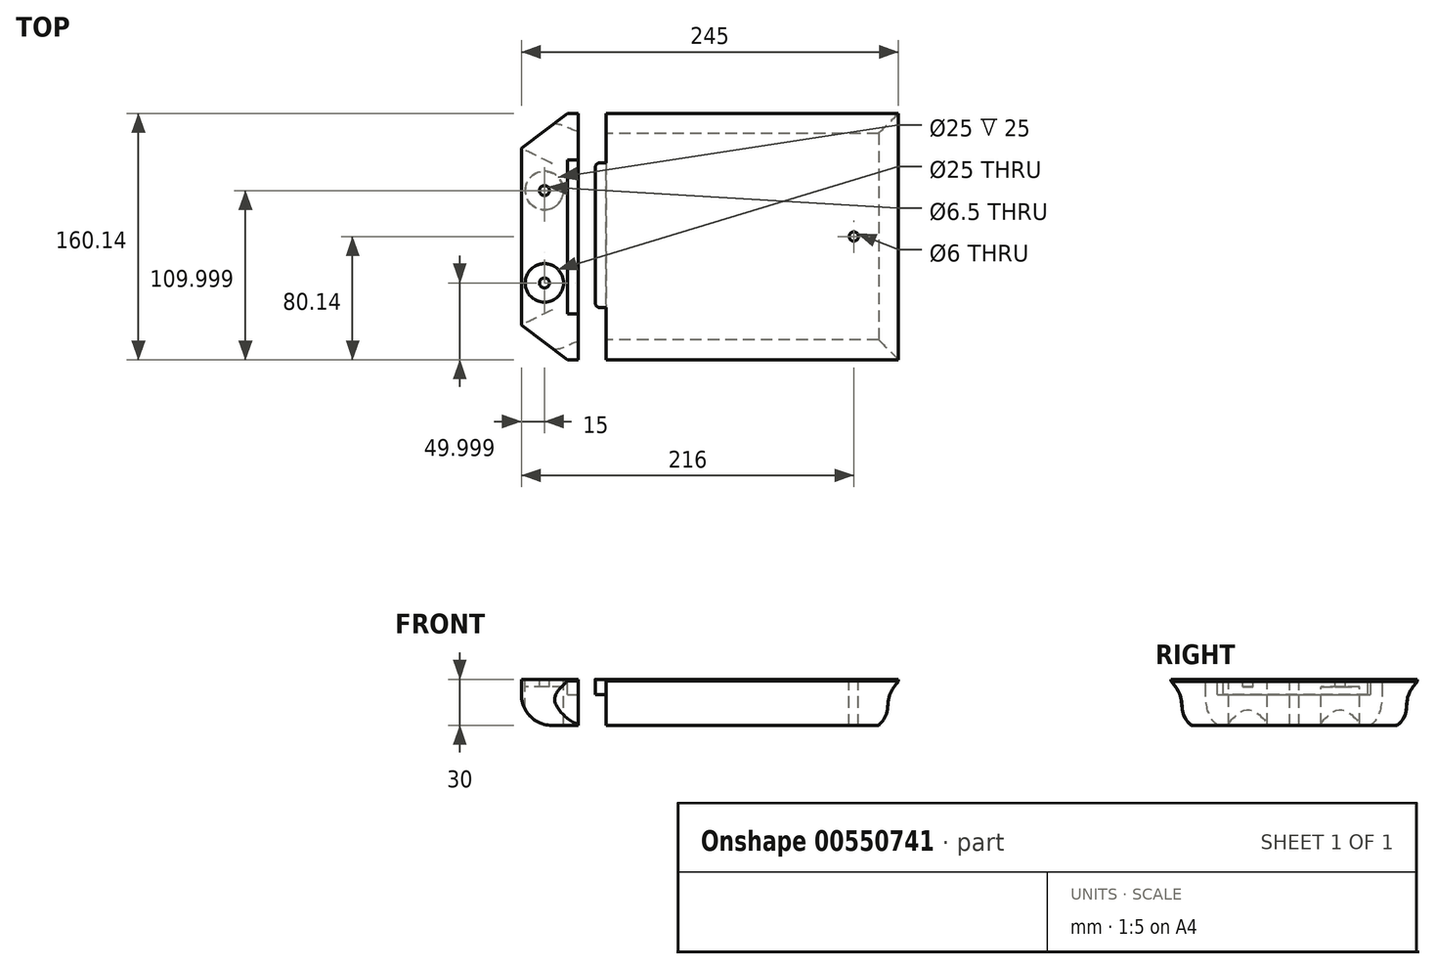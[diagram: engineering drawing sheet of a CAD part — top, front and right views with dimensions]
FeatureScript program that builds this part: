
annotation { "Feature Type Name" : "Feature", "Feature Type Description" : "" }
export const myFeature = defineFeature(function(context is Context, id is Id, definition is map)
    precondition{}
    {
        {
            var Q0;
            Q0=qCreatedBy(makeId("Top.planeOp"),FACE);
            var sketch = newSketch(context, id + "F0", { "sketchPlane" : qUnion([Q0])});
            skLineSegment(sketch, "E0.bottom", {"start": v(-97.5, 80) * mm, "end": v(92.5, 80) * mm});
            skLineSegment(sketch, "E0.top", {"start": v(-92.5, 0) * mm, "end": v(92.5, 0) * mm, "construction": true});
            skLineSegment(sketch, "E0.right", {"start": v(92.5, 80) * mm, "end": v(92.5, 0) * mm});
            skLineSegment(sketch, "E1.bottom", {"start": v(-82.5, 63.5) * mm, "end": v(77.5, 63.5) * mm});
            skLineSegment(sketch, "E1.left", {"start": v(-97.5, 63.5) * mm, "end": v(-97.5, -5) * mm});
            skLineSegment(sketch, "E1.right", {"start": v(77.5, 63.5) * mm, "end": v(77.5, 0) * mm});
            skLineSegment(sketch, "E2.right", {"start": v(49.5, 65) * mm, "end": v(49.5, 0) * mm});
            skLineSegment(sketch, "E3.MirrorCS", {"start": v(-82.5, -63.5) * mm, "end": v(77.5, -63.5) * mm});
            skLineSegment(sketch, "E4.MirrorCS", {"start": v(-97.5, -63.5) * mm, "end": v(-97.5, 5) * mm});
            skLineSegment(sketch, "E5.MirrorCS", {"start": v(-97.5, -80) * mm, "end": v(92.5, -80) * mm});
            skLineSegment(sketch, "E6.MirrorCS", {"start": v(92.5, -80) * mm, "end": v(92.5, 0) * mm});
            skLineSegment(sketch, "E7.MirrorCS", {"start": v(57.5, -4.97) * mm, "end": v(66.5, -4.97) * mm});
            skLineSegment(sketch, "E8.MirrorCS", {"start": v(54.5, -13.97) * mm, "end": v(54.5, -9.97) * mm});
            skLineSegment(sketch, "E9.MirrorCS", {"start": v(77.5, -63.5) * mm, "end": v(77.5, 0) * mm});
            skLineSegment(sketch, "E10.MirrorCS", {"start": v(69.5, -13.97) * mm, "end": v(69.5, -9.97) * mm});
            skLineSegment(sketch, "E11.MirrorCS", {"start": v(49.5, -63.5) * mm, "end": v(49.5, 0) * mm});
            skLineSegment(sketch, "E12", {"start": v(-97.5, -63.5) * mm, "end": v(-97.5, -80) * mm});
            skLineSegment(sketch, "E13", {"start": v(-97.5, 63.5) * mm, "end": v(-97.5, 80) * mm});
            skLineSegment(sketch, "E14.left", {"start": v(-152.5, 57.36) * mm, "end": v(-152.5, 9.86) * mm});
            skCircle(sketch, "E15", {"center": v(-137.5, 29.86) * mm, "radius": 3.25 * mm});
            skLineSegment(sketch, "E16.left", {"start": v(-122.5, 79.86) * mm, "end": v(-122.5, -0.14) * mm});
            skCircle(sketch, "E17.MirrorC", {"center": v(-137.5, -30.14) * mm, "radius": 3.25 * mm});
            skLineSegment(sketch, "E18.MirrorCS", {"start": v(-122.5, -80.14) * mm, "end": v(-122.5, -10.14) * mm});
            skLineSegment(sketch, "E19.MirrorCS", {"start": v(-152.5, -57.64) * mm, "end": v(-152.5, -10.14) * mm});
            skCircle(sketch, "E20", {"center": v(-137.5, 29.86) * mm, "radius": 12.5 * mm});
            skCircle(sketch, "E21.MirrorC", {"center": v(-137.5, -30.14) * mm, "radius": 12.5 * mm});
            skPoint(sketch, "E22", {"position": v(-122.5, -50.14) * mm});
            skLineSegment(sketch, "E23", {"start": v(-122.5, -50.14) * mm, "end": v(-117.5, -50.14) * mm});
            skPoint(sketch, "E24", {"position": v(-122.5, 49.86) * mm});
            skLineSegment(sketch, "E25", {"start": v(-122.5, 49.86) * mm, "end": v(-117.5, 49.86) * mm});
            skLineSegment(sketch, "E26", {"start": v(-104.5, -30.14) * mm, "end": v(-104.5, 44.86) * mm});
            skLineSegment(sketch, "E27", {"start": v(-117.5, -50.14) * mm, "end": v(-115.5, -50.14) * mm});
            skLineSegment(sketch, "E28", {"start": v(-115.5, -50.14) * mm, "end": v(-115.5, -80.14) * mm});
            skLineSegment(sketch, "E29", {"start": v(-115.5, -50.14) * mm, "end": v(-115.5, 79.86) * mm});
            skLineSegment(sketch, "E30", {"start": v(-117.5, 49.86) * mm, "end": v(-115.5, 49.86) * mm});
            skLineSegment(sketch, "E31", {"start": v(-97.5, -80) * mm, "end": v(-82.5, -80) * mm});
            skLineSegment(sketch, "E32", {"start": v(-82.5, -80) * mm, "end": v(-82.5, 63.5) * mm});
            skLineSegment(sketch, "E33", {"start": v(57.5, -16.97) * mm, "end": v(66.5, -16.97) * mm});
            skLineSegment(sketch, "E34", {"start": v(57.5, -6.97) * mm, "end": v(66.5, -6.97) * mm});
            skLineSegment(sketch, "E35", {"start": v(57.5, -18.97) * mm, "end": v(66.5, -18.97) * mm});
            skLineSegment(sketch, "E36", {"start": v(56.02, -30.47) * mm, "end": v(63.02, -30.47) * mm});
            skLineSegment(sketch, "E37", {"start": v(54.5, -63.15) * mm, "end": v(66.5, -63.15) * mm});
            skLineSegment(sketch, "E38", {"start": v(69.5, -58.47) * mm, "end": v(69.5, -51.47) * mm});
            skArc(sketch, "E39.filletArc", {"start": v(57.5, -4.97) * mm, "mid": v(55.38, -5.85) * mm, "end": v(54.5, -7.97) * mm});
            skArc(sketch, "E40.filletArc", {"start": v(69.5, -7.97) * mm, "mid": v(68.62, -5.85) * mm, "end": v(66.5, -4.97) * mm});
            skLineSegment(sketch, "E41", {"start": v(54.5, -45) * mm, "end": v(54.5, -27.47) * mm});
            skLineSegment(sketch, "E42", {"start": v(69.5, -27.47) * mm, "end": v(69.5, -45) * mm});
            skCircle(sketch, "E43", {"center": v(62, -55.5) * mm, "radius": 2.55 * mm});
            skCircle(sketch, "E44.MirrorC", {"center": v(62, 25.97) * mm, "radius": 2.55 * mm});
            skLineSegment(sketch, "E45.MirrorCS", {"start": v(57.5, 6.97) * mm, "end": v(66.5, 6.97) * mm});
            skLineSegment(sketch, "E46.MirrorCS", {"start": v(69.5, 13.97) * mm, "end": v(69.5, 9.97) * mm});
            skLineSegment(sketch, "E47.MirrorCS", {"start": v(57.5, 16.97) * mm, "end": v(66.5, 16.97) * mm});
            skLineSegment(sketch, "E48.MirrorCS", {"start": v(57.5, 4.97) * mm, "end": v(66.5, 4.97) * mm});
            skLineSegment(sketch, "E49.MirrorCS", {"start": v(57.5, 18.97) * mm, "end": v(66.5, 18.97) * mm});
            skLineSegment(sketch, "E50.MirrorCS", {"start": v(54.5, 44.51) * mm, "end": v(54.5, 27.47) * mm});
            skLineSegment(sketch, "E51.MirrorCS", {"start": v(69.5, 27.47) * mm, "end": v(69.5, 44.51) * mm});
            skLineSegment(sketch, "E52.MirrorCS", {"start": v(54.5, 15.97) * mm, "end": v(54.5, 9.97) * mm});
            skLineSegment(sketch, "E53.MirrorCS", {"start": v(69.5, 15.97) * mm, "end": v(69.5, 7.97) * mm});
            skLineSegment(sketch, "E54.MirrorCS", {"start": v(57.5, 6.97) * mm, "end": v(65.5, 6.97) * mm});
            skLineSegment(sketch, "E55.MirrorCS", {"start": v(54.5, 16.97) * mm, "end": v(54.67, 16.97) * mm});
            skLineSegment(sketch, "E56.MirrorCS", {"start": v(54.5, 13.97) * mm, "end": v(54.5, 7.97) * mm});
            skLineSegment(sketch, "E57.MirrorCS", {"start": v(57.5, 18.97) * mm, "end": v(65.5, 18.97) * mm});
            skLineSegment(sketch, "E58", {"start": v(57.5, 47.51) * mm, "end": v(66.5, 47.51) * mm});
            skLineSegment(sketch, "E59", {"start": v(54.5, -49.9) * mm, "end": v(67.5, -49.9) * mm});
            skLineSegment(sketch, "E60", {"start": v(-122.5, 79.86) * mm, "end": v(-115.5, 79.86) * mm});
            skLineSegment(sketch, "E61", {"start": v(-122.5, -80.14) * mm, "end": v(-115.5, -80.14) * mm});
            skLineSegment(sketch, "E62", {"start": v(-122.5, 79.86) * mm, "end": v(-152.5, 57.36) * mm});
            skLineSegment(sketch, "E63", {"start": v(-122.5, -80.14) * mm, "end": v(-152.5, -57.64) * mm});
            skLineSegment(sketch, "E64", {"start": v(49.5, 41) * mm, "end": v(54.5, 41) * mm});
            skLineSegment(sketch, "E65", {"start": v(49.5, 29) * mm, "end": v(54.5, 29) * mm});
            skLineSegment(sketch, "E66", {"start": v(77.5, 0) * mm, "end": v(49.5, 0) * mm});
            skCircle(sketch, "E67", {"center": v(63.5, 0) * mm, "radius": 3 * mm});
            skLineSegment(sketch, "E68", {"start": v(57.9, 23.83) * mm, "end": v(57.9, 28.1) * mm});
            skLineSegment(sketch, "E69", {"start": v(66.1, 23.83) * mm, "end": v(66.1, 28.1) * mm});
            skLineSegment(sketch, "E70", {"start": v(60.28, 21.42) * mm, "end": v(57.9, 23.08) * mm});
            skLineSegment(sketch, "E71", {"start": v(63.72, 21.42) * mm, "end": v(66.1, 23.08) * mm});
            skLineSegment(sketch, "E72", {"start": v(63.72, 30.52) * mm, "end": v(66.1, 28.86) * mm});
            skLineSegment(sketch, "E73", {"start": v(60.28, 30.52) * mm, "end": v(57.9, 28.86) * mm});
            skLineSegment(sketch, "E74", {"start": v(57.9, -57.64) * mm, "end": v(57.9, -53.37) * mm});
            skLineSegment(sketch, "E75", {"start": v(66.1, -57.64) * mm, "end": v(66.1, -53.37) * mm});
            skLineSegment(sketch, "E76", {"start": v(60.28, -60.05) * mm, "end": v(57.9, -58.4) * mm});
            skLineSegment(sketch, "E77", {"start": v(63.72, -60.05) * mm, "end": v(66.1, -58.4) * mm});
            skLineSegment(sketch, "E78", {"start": v(63.72, -50.94) * mm, "end": v(66.1, -52.6) * mm});
            skLineSegment(sketch, "E79", {"start": v(60.28, -50.94) * mm, "end": v(57.9, -52.6) * mm});
            skCircle(sketch, "E80.MirrorC", {"center": v(62, -24.47) * mm, "radius": 2.55 * mm});
            skLineSegment(sketch, "E81", {"start": v(57.9, -26.61) * mm, "end": v(57.9, -22.33) * mm});
            skLineSegment(sketch, "E82", {"start": v(66.1, -26.61) * mm, "end": v(66.1, -22.33) * mm});
            skLineSegment(sketch, "E83", {"start": v(60.28, -29.02) * mm, "end": v(57.9, -27.36) * mm});
            skLineSegment(sketch, "E84", {"start": v(63.72, -29.02) * mm, "end": v(66.1, -27.36) * mm});
            skLineSegment(sketch, "E85", {"start": v(63.72, -19.92) * mm, "end": v(66.1, -21.58) * mm});
            skLineSegment(sketch, "E86", {"start": v(60.28, -19.92) * mm, "end": v(57.9, -21.58) * mm});
            skArc(sketch, "E87.filletArc", {"start": v(69.5, 44.51) * mm, "mid": v(68.62, 46.63) * mm, "end": v(66.5, 47.51) * mm});
            skArc(sketch, "E88.filletArc", {"start": v(57.5, 47.51) * mm, "mid": v(55.38, 46.63) * mm, "end": v(54.5, 44.51) * mm});
            skArc(sketch, "E89.filletArc", {"start": v(54.5, 9.97) * mm, "mid": v(55.38, 7.85) * mm, "end": v(57.5, 6.97) * mm});
            skArc(sketch, "E90.filletArc", {"start": v(66.5, 6.97) * mm, "mid": v(68.62, 7.85) * mm, "end": v(69.5, 9.97) * mm});
            skArc(sketch, "E91.filletArc", {"start": v(57.5, 16.97) * mm, "mid": v(55.38, 16.1) * mm, "end": v(54.5, 13.97) * mm});
            skArc(sketch, "E92.filletArc", {"start": v(69.5, 13.97) * mm, "mid": v(68.62, 16.1) * mm, "end": v(66.5, 16.97) * mm});
            skArc(sketch, "E93.filletArc", {"start": v(57.5, 18.97) * mm, "mid": v(55.38, 18.1) * mm, "end": v(54.5, 15.97) * mm});
            skArc(sketch, "E94.filletArc", {"start": v(69.5, 15.97) * mm, "mid": v(68.62, 18.1) * mm, "end": v(66.5, 18.97) * mm});
            skArc(sketch, "E95.filletArc", {"start": v(54.5, -13.97) * mm, "mid": v(55.38, -16.1) * mm, "end": v(57.5, -16.97) * mm});
            skArc(sketch, "E96.filletArc", {"start": v(66.5, -16.97) * mm, "mid": v(68.62, -16.1) * mm, "end": v(69.5, -13.97) * mm});
            skLineSegment(sketch, "E97", {"start": v(54.5, -13.97) * mm, "end": v(54.5, -15.97) * mm});
            skLineSegment(sketch, "E98", {"start": v(69.5, -13.97) * mm, "end": v(69.5, -15.97) * mm});
            skArc(sketch, "E99.filletArc", {"start": v(54.5, -15.97) * mm, "mid": v(55.38, -18.1) * mm, "end": v(57.5, -18.97) * mm});
            skArc(sketch, "E100.filletArc", {"start": v(66.5, -18.97) * mm, "mid": v(68.62, -18.1) * mm, "end": v(69.5, -15.97) * mm});
            skLineSegment(sketch, "E101", {"start": v(54.5, -15.97) * mm, "end": v(54.5, -25.97) * mm});
            skLineSegment(sketch, "E102", {"start": v(69.5, -25.97) * mm, "end": v(69.5, -15.97) * mm});
            skArc(sketch, "E103.filletArc", {"start": v(57.5, -6.97) * mm, "mid": v(55.38, -7.85) * mm, "end": v(54.5, -9.97) * mm});
            skArc(sketch, "E104.filletArc", {"start": v(69.5, -9.97) * mm, "mid": v(68.62, -7.85) * mm, "end": v(66.5, -6.97) * mm});
            skLineSegment(sketch, "E105", {"start": v(54.5, -9.97) * mm, "end": v(54.5, -7.97) * mm});
            skLineSegment(sketch, "E106", {"start": v(69.5, -9.97) * mm, "end": v(69.5, -7.97) * mm});
            skLineSegment(sketch, "E107", {"start": v(54.5, 27.47) * mm, "end": v(54.5, 13.97) * mm});
            skLineSegment(sketch, "E108", {"start": v(69.5, 27.47) * mm, "end": v(69.5, 15.97) * mm});
            skLineSegment(sketch, "E109", {"start": v(69.5, -45) * mm, "end": v(69.5, -51.47) * mm});
            skLineSegment(sketch, "E110", {"start": v(69.5, -58.47) * mm, "end": v(69.5, -60.15) * mm});
            skArc(sketch, "E111.filletArc", {"start": v(66.5, -63.15) * mm, "mid": v(68.62, -62.27) * mm, "end": v(69.5, -60.15) * mm});
            skLineSegment(sketch, "E112", {"start": v(-122.5, -10.14) * mm, "end": v(-122.5, -0.14) * mm});
            skLineSegment(sketch, "E113", {"start": v(-152.5, -10.14) * mm, "end": v(-152.5, 9.86) * mm});
            skLineSegment(sketch, "E114", {"start": v(-122.5, -50.14) * mm, "end": v(-152.5, -50.14) * mm});
            skLineSegment(sketch, "E115", {"start": v(-122.5, 49.86) * mm, "end": v(-152.5, 49.86) * mm});
            skLineSegment(sketch, "E116", {"start": v(46.5, -63.5) * mm, "end": v(46.5, 63.5) * mm});
            skLineSegment(sketch, "E117", {"start": v(56.02, -30.47) * mm, "end": v(54.5, -30.47) * mm});
            skLineSegment(sketch, "E118", {"start": v(63.02, -30.47) * mm, "end": v(69.5, -30.47) * mm});
            skLineSegment(sketch, "E119", {"start": v(49.5, 29) * mm, "end": v(46.5, 29) * mm});
            skLineSegment(sketch, "E120", {"start": v(49.5, 41) * mm, "end": v(46.5, 41) * mm});
            skLineSegment(sketch, "E121", {"start": v(50.5, -49.9) * mm, "end": v(47.5, -49.9) * mm});
            skLineSegment(sketch, "E122", {"start": v(65.5, -49.9) * mm, "end": v(55.5, -49.9) * mm});
            skLineSegment(sketch, "E123", {"start": v(54.5, -30.47) * mm, "end": v(69.5, -30.47) * mm});
            skLineSegment(sketch, "E124", {"start": v(69.5, -30.47) * mm, "end": v(69.5, -50) * mm});
            skLineSegment(sketch, "E125", {"start": v(-101.5, 47.86) * mm, "end": v(-97.5, 47.86) * mm});
            skLineSegment(sketch, "E126", {"start": v(-104.5, -30.14) * mm, "end": v(-104.5, -43.14) * mm});
            skLineSegment(sketch, "E127", {"start": v(-101.5, -46.14) * mm, "end": v(-97.5, -46.14) * mm});
            skPoint(sketch, "E128.end.orphan", {"position": v(-97.5, 59.86) * mm});
            skLineSegment(sketch, "E129", {"start": v(47.5, -49.9) * mm, "end": v(46.5, -49.9) * mm});
            skPoint(sketch, "E130", {"position": v(-90, -50) * mm});
            skLineSegment(sketch, "E131", {"start": v(-93.5, -52.14) * mm, "end": v(-93.5, -47.87) * mm});
            skLineSegment(sketch, "E132", {"start": v(-86.5, -52.14) * mm, "end": v(-86.5, -47.87) * mm});
            skLineSegment(sketch, "E133", {"start": v(-91.72, -54.89) * mm, "end": v(-93.5, -53.64) * mm});
            skLineSegment(sketch, "E134", {"start": v(-88.28, -45.12) * mm, "end": v(-86.5, -46.37) * mm});
            skLineSegment(sketch, "E135", {"start": v(-91.72, -45.12) * mm, "end": v(-93.5, -46.37) * mm});
            skLineSegment(sketch, "E136", {"start": v(-86.5, -53.64) * mm, "end": v(-88.28, -54.89) * mm});
            skPoint(sketch, "E137.newPointA", {"position": v(66.5, 4.97) * mm});
            skArc(sketch, "E137.filletArc", {"start": v(66.5, 4.97) * mm, "mid": v(68.62, 5.85) * mm, "end": v(69.5, 7.97) * mm});
            skPoint(sketch, "E138.MirrorCS.start.orphan", {"position": v(69.5, 7.97) * mm});
            skLineSegment(sketch, "E139.trimOffspring", {"start": v(57.5, 16.97) * mm, "end": v(64.5, 16.97) * mm});
            skPoint(sketch, "E140.newPointA", {"position": v(57.5, 4.97) * mm});
            skArc(sketch, "E140.filletArc", {"start": v(54.5, 7.97) * mm, "mid": v(55.38, 5.85) * mm, "end": v(57.5, 4.97) * mm});
            skPoint(sketch, "E141.MirrorCS.end.orphan", {"position": v(54.5, 7.97) * mm});
            skLineSegment(sketch, "E142", {"start": v(54.5, -45) * mm, "end": v(54.5, -63.5) * mm});
            skLineSegment(sketch, "E143", {"start": v(69.5, -25.97) * mm, "end": v(69.5, -27.47) * mm});
            skLineSegment(sketch, "E144", {"start": v(54.5, -25.97) * mm, "end": v(54.5, -27.47) * mm});
            skArc(sketch, "E145.filletArc", {"start": v(-104.5, -43.14) * mm, "mid": v(-103.62, -45.26) * mm, "end": v(-101.5, -46.14) * mm});
            skArc(sketch, "E146.filletArc", {"start": v(-101.5, 47.86) * mm, "mid": v(-103.62, 46.98) * mm, "end": v(-104.5, 44.86) * mm});
            skLineSegment(sketch, "E147", {"start": v(-93.5, -47.87) * mm, "end": v(-93.5, -46.37) * mm});
            skLineSegment(sketch, "E148", {"start": v(-86.5, -47.87) * mm, "end": v(-86.5, -46.37) * mm});
            skLineSegment(sketch, "E149", {"start": v(-93.5, -52.14) * mm, "end": v(-93.5, -53.64) * mm});
            skLineSegment(sketch, "E150", {"start": v(-86.5, -52.14) * mm, "end": v(-86.5, -53.64) * mm});
            skLineSegment(sketch, "E151.MirrorCS", {"start": v(-86.5, 52.14) * mm, "end": v(-86.5, 47.87) * mm});
            skLineSegment(sketch, "E152.MirrorCS", {"start": v(-93.5, 47.87) * mm, "end": v(-93.5, 46.37) * mm});
            skLineSegment(sketch, "E153.MirrorCS", {"start": v(-86.5, 47.87) * mm, "end": v(-86.5, 46.37) * mm});
            skLineSegment(sketch, "E154.MirrorCS", {"start": v(-93.5, 52.14) * mm, "end": v(-93.5, 47.87) * mm});
            skLineSegment(sketch, "E155.MirrorCS", {"start": v(-93.5, 52.14) * mm, "end": v(-93.5, 53.64) * mm});
            skLineSegment(sketch, "E156.MirrorCS", {"start": v(-86.5, 52.14) * mm, "end": v(-86.5, 53.64) * mm});
            skLineSegment(sketch, "E157.MirrorCS", {"start": v(-91.72, 45.12) * mm, "end": v(-93.5, 46.37) * mm});
            skPoint(sketch, "E158.MirrorP", {"position": v(-90, 50) * mm});
            skLineSegment(sketch, "E159.MirrorCS", {"start": v(-86.5, 53.64) * mm, "end": v(-88.28, 54.89) * mm});
            skLineSegment(sketch, "E160.MirrorCS", {"start": v(-88.28, 45.12) * mm, "end": v(-86.5, 46.37) * mm});
            skLineSegment(sketch, "E161.MirrorCS", {"start": v(-91.72, 54.89) * mm, "end": v(-93.5, 53.64) * mm});
            skLineSegment(sketch, "E162", {"start": v(54.5, -63.15) * mm, "end": v(49.5, -63.15) * mm});
            skLineSegment(sketch, "E163", {"start": v(49.5, -63.15) * mm, "end": v(46.5, -63.15) * mm});
            skArc(sketch, "E164.filletArc", {"start": v(63.72, -50.94) * mm, "mid": v(62, -50.4) * mm, "end": v(60.28, -50.94) * mm});
            skArc(sketch, "E165.filletArc", {"start": v(60.28, -60.05) * mm, "mid": v(62, -60.6) * mm, "end": v(63.72, -60.05) * mm});
            skLineSegment(sketch, "E166", {"start": v(57.9, -52.6) * mm, "end": v(57.9, -53.37) * mm});
            skLineSegment(sketch, "E167", {"start": v(66.1, -52.6) * mm, "end": v(66.1, -53.37) * mm});
            skLineSegment(sketch, "E168", {"start": v(57.9, -58.4) * mm, "end": v(57.9, -57.64) * mm});
            skLineSegment(sketch, "E169", {"start": v(66.1, -58.4) * mm, "end": v(66.1, -57.64) * mm});
            skArc(sketch, "E170.filletArc", {"start": v(63.72, -19.92) * mm, "mid": v(62, -19.38) * mm, "end": v(60.28, -19.92) * mm});
            skArc(sketch, "E171.filletArc", {"start": v(60.28, -29.02) * mm, "mid": v(62, -29.56) * mm, "end": v(63.72, -29.02) * mm});
            skLineSegment(sketch, "E172", {"start": v(57.9, -21.58) * mm, "end": v(57.9, -22.33) * mm});
            skLineSegment(sketch, "E173", {"start": v(66.1, -21.58) * mm, "end": v(66.1, -22.33) * mm});
            skLineSegment(sketch, "E174", {"start": v(57.9, -26.61) * mm, "end": v(57.9, -27.36) * mm});
            skLineSegment(sketch, "E175", {"start": v(66.1, -26.61) * mm, "end": v(66.1, -27.36) * mm});
            skArc(sketch, "E176.filletArc", {"start": v(63.72, 30.52) * mm, "mid": v(62, 31.06) * mm, "end": v(60.28, 30.52) * mm});
            skArc(sketch, "E177.filletArc", {"start": v(60.28, 21.42) * mm, "mid": v(62, 20.88) * mm, "end": v(63.72, 21.42) * mm});
            skLineSegment(sketch, "E178", {"start": v(57.9, 23.83) * mm, "end": v(57.9, 23.08) * mm});
            skLineSegment(sketch, "E179", {"start": v(66.1, 23.83) * mm, "end": v(66.1, 23.08) * mm});
            skLineSegment(sketch, "E180", {"start": v(57.9, 28.86) * mm, "end": v(57.9, 28.1) * mm});
            skLineSegment(sketch, "E181", {"start": v(66.1, 28.86) * mm, "end": v(66.1, 28.1) * mm});
            skArc(sketch, "E182.filletArc", {"start": v(-88.28, 54.89) * mm, "mid": v(-90, 55.43) * mm, "end": v(-91.72, 54.89) * mm});
            skArc(sketch, "E183.filletArc", {"start": v(-91.72, 45.12) * mm, "mid": v(-90, 44.58) * mm, "end": v(-88.28, 45.12) * mm});
            skArc(sketch, "E184.filletArc", {"start": v(-91.72, -54.89) * mm, "mid": v(-90, -55.43) * mm, "end": v(-88.28, -54.89) * mm});
            skArc(sketch, "E185.filletArc", {"start": v(-88.28, -45.12) * mm, "mid": v(-90, -44.58) * mm, "end": v(-91.72, -45.12) * mm});
            skLineSegment(sketch, "E186", {"start": v(67.5, -49.9) * mm, "end": v(69.5, -49.9) * mm});
            skLineSegment(sketch, "E187", {"start": v(50.5, -49.9) * mm, "end": v(54.5, -49.9) * mm});
            skPoint(sketch, "E188", {"position": v(73.5, -24.16) * mm});
            skLineSegment(sketch, "E189", {"start": v(70, -26.3) * mm, "end": v(70, -22.03) * mm});
            skLineSegment(sketch, "E190", {"start": v(77, -26.3) * mm, "end": v(77, -22.03) * mm});
            skLineSegment(sketch, "E191", {"start": v(71.77, -29.05) * mm, "end": v(70, -27.8) * mm});
            skLineSegment(sketch, "E192", {"start": v(75.2, -19.28) * mm, "end": v(77, -20.53) * mm});
            skLineSegment(sketch, "E193", {"start": v(71.77, -19.28) * mm, "end": v(70, -20.53) * mm});
            skLineSegment(sketch, "E194", {"start": v(77, -27.8) * mm, "end": v(75.2, -29.05) * mm});
            skLineSegment(sketch, "E195", {"start": v(70, -22.03) * mm, "end": v(70, -20.53) * mm});
            skLineSegment(sketch, "E196", {"start": v(77, -22.03) * mm, "end": v(77, -20.53) * mm});
            skLineSegment(sketch, "E197", {"start": v(70, -26.3) * mm, "end": v(70, -27.8) * mm});
            skLineSegment(sketch, "E198", {"start": v(77, -26.3) * mm, "end": v(77, -27.8) * mm});
            skArc(sketch, "E199.filletArc", {"start": v(71.77, -29.05) * mm, "mid": v(73.5, -29.59) * mm, "end": v(75.2, -29.05) * mm});
            skArc(sketch, "E200.filletArc", {"start": v(75.2, -19.28) * mm, "mid": v(73.5, -18.74) * mm, "end": v(71.77, -19.28) * mm});
            skLineSegment(sketch, "E201.MirrorCS", {"start": v(70, 26.3) * mm, "end": v(70, 27.8) * mm});
            skLineSegment(sketch, "E202.MirrorCS", {"start": v(77, 26.3) * mm, "end": v(77, 22.03) * mm});
            skLineSegment(sketch, "E203.MirrorCS", {"start": v(77, 27.8) * mm, "end": v(75.2, 29.05) * mm});
            skLineSegment(sketch, "E204.MirrorCS", {"start": v(70, 22.03) * mm, "end": v(70, 20.53) * mm});
            skArc(sketch, "E205.MirrorCS", {"start": v(71.77, 29.05) * mm, "mid": v(73.5, 29.59) * mm, "end": v(75.2, 29.05) * mm});
            skLineSegment(sketch, "E206.MirrorCS", {"start": v(77, 22.03) * mm, "end": v(77, 20.53) * mm});
            skLineSegment(sketch, "E207.MirrorCS", {"start": v(70, 26.3) * mm, "end": v(70, 22.03) * mm});
            skLineSegment(sketch, "E208.MirrorCS", {"start": v(71.77, 29.05) * mm, "end": v(70, 27.8) * mm});
            skLineSegment(sketch, "E209.MirrorCS", {"start": v(75.2, 19.28) * mm, "end": v(77, 20.53) * mm});
            skLineSegment(sketch, "E210.MirrorCS", {"start": v(71.77, 19.28) * mm, "end": v(70, 20.53) * mm});
            skArc(sketch, "E211.MirrorCS", {"start": v(75.2, 19.28) * mm, "mid": v(73.5, 18.74) * mm, "end": v(71.77, 19.28) * mm});
            skPoint(sketch, "E212.MirrorP", {"position": v(73.5, 24.16) * mm});
            skLineSegment(sketch, "E213.MirrorCS", {"start": v(77, 26.3) * mm, "end": v(77, 27.8) * mm});
            skSolve(sketch);
        }
        {
            var Q0;
            {var subQ6=sQuery(id+"F0.wireOp",EDGE,"RdLYVHK0-ZMMy-n2T9-vo5N-ViF6aoFnglOa");Q0=makeQuery(id+"F0.imprint","IMPRINT",FACE,{"disambiguationData":[TD([[makeQuery(id+"F0.imprint","IMPRINT",EDGE,{"derivedFrom":subQ6}),-1.0]])]});}
            var Q1;
            {var subQ6=sQuery(id+"F0.wireOp",EDGE,"E59");Q1=makeQuery(id+"F0.imprint","IMPRINT",FACE,{"disambiguationData":[TD([[makeQuery(id+"F0.imprint","IMPRINT",EDGE,{"derivedFrom":subQ6}),-1.0]])]});}
            var Q2;
            {var subQ8=sQuery(id+"F0.wireOp",EDGE,"E51.MirrorCS");Q2=makeQuery(id+"F0.imprint","IMPRINT",FACE,{"disambiguationData":[TD([[makeQuery(id+"F0.imprint","IMPRINT",EDGE,{"derivedFrom":subQ8}),1.0]])]});}
            var Q3;
            Q3=makeQuery(id+"F0.imprint","IMPRINT",FACE,{"disambiguationData":[TD([[makeQuery(id+"F0.imprint","IMPRINT",EDGE,{"derivedFrom":sQuery(id+"F0.wireOp",EDGE,"E36")}),-1.0]])]});
            var Q4;
            {var subQ8=sQuery(id+"F0.wireOp",EDGE,"E93.filletArc");Q4=makeQuery(id+"F0.imprint","IMPRINT",FACE,{"disambiguationData":[TD([[makeQuery(id+"F0.imprint","IMPRINT",EDGE,{"derivedFrom":subQ8}),1.0]])]});}
            var Q5;
            {var subQ5=sQuery(id+"F0.wireOp",EDGE,"E37");Q5=makeQuery(id+"F0.imprint","IMPRINT",FACE,{"disambiguationData":[TD([[makeQuery(id+"F0.imprint","IMPRINT",EDGE,{"derivedFrom":subQ5}),1.0]])]});}
            var Q6;
            Q6=makeQuery(id+"F0.imprint","IMPRINT",FACE,{"disambiguationData":[TD([[makeQuery(id+"F0.imprint","IMPRINT",EDGE,{"derivedFrom":sQuery(id+"F0.wireOp",EDGE,"E7.MirrorCS")}),-1.0]])]});
            var Q7;
            {var subQ5=sQuery(id+"F0.wireOp",EDGE,"6d39de08-ad94-4231-b662-17a660603f591.MirrorCS");Q7=makeQuery(id+"F0.imprint","IMPRINT",FACE,{"disambiguationData":[TD([[makeQuery(id+"F0.imprint","IMPRINT",EDGE,{"derivedFrom":subQ5}),-1.0]])]});}
            var Q8;
            Q8=makeQuery(id+"F0.imprint","IMPRINT",FACE,{"disambiguationData":[TD([[makeQuery(id+"F0.imprint","IMPRINT",EDGE,{"derivedFrom":sQuery(id+"F0.wireOp",EDGE,"E68")}),-1.0]])]});
            var Q9;
            {var subQ4=sQuery(id+"F0.wireOp",EDGE,"E74");Q9=makeQuery(id+"F0.imprint","IMPRINT",FACE,{"disambiguationData":[TD([[makeQuery(id+"F0.imprint","IMPRINT",EDGE,{"derivedFrom":subQ4}),-1.0]])]});}
            var Q10;
            {var subQ0=sQuery(id+"F0.wireOp",EDGE,"6d39de08-ad94-4231-b662-17a660603f594.MirrorC");var subQ1=sQuery(id+"F0.wireOp",EDGE,"E44.MirrorC");var subQ2=makeQuery(id+"F0.imprint","INTERSECT",VERTEX,{"disambiguationData":[OD(0.0)],"derivedFrom":[subQ1,subQ0]});Q10=makeQuery(id+"F0.imprint","IMPRINT",FACE,{"disambiguationData":[TD([[makeQuery(id+"F0.imprint","IMPRINT",EDGE,{"disambiguationData":[TD([[subQ2,-1.0]])],"derivedFrom":subQ1}),-1.0]])]});}
            var Q11;
            {var subQ5=sQuery(id+"F0.wireOp",EDGE,"2Ry4WlIC-CQQb-5CF8-FWkS-usfLcIxYfUWP");Q11=makeQuery(id+"F0.imprint","IMPRINT",FACE,{"disambiguationData":[TD([[makeQuery(id+"F0.imprint","IMPRINT",EDGE,{"derivedFrom":subQ5}),-1.0]])]});}
            var Q12;
            Q12=makeQuery(id+"F0.imprint","IMPRINT",FACE,{"disambiguationData":[TD([[makeQuery(id+"F0.imprint","IMPRINT",EDGE,{"derivedFrom":sQuery(id+"F0.wireOp",EDGE,"E80.MirrorC")}),1.0]])]});
            var Q13;
            Q13=makeQuery(id+"F0.imprint","IMPRINT",FACE,{"disambiguationData":[TD([[makeQuery(id+"F0.imprint","IMPRINT",EDGE,{"derivedFrom":sQuery(id+"F0.wireOp",EDGE,"E80.MirrorC")}),-1.0]])]});
            var Q14;
            {var subQ0=sQuery(id+"F0.wireOp",EDGE,"da70cb73-bd24-4d72-8de4-aa27c8984207.MirrorC");var subQ1=sQuery(id+"F0.wireOp",EDGE,"E43");var subQ2=makeQuery(id+"F0.imprint","INTERSECT",VERTEX,{"disambiguationData":[OD(0.0)],"derivedFrom":[subQ1,subQ0]});Q14=makeQuery(id+"F0.imprint","IMPRINT",FACE,{"disambiguationData":[TD([[makeQuery(id+"F0.imprint","IMPRINT",EDGE,{"disambiguationData":[TD([[subQ2,-1.0]])],"derivedFrom":subQ1}),1.0]])]});}
            var Q15;
            {var subQ0=sQuery(id+"F0.wireOp",EDGE,"da70cb73-bd24-4d72-8de4-aa27c8984207.MirrorC");var subQ1=sQuery(id+"F0.wireOp",EDGE,"E43");var subQ2=makeQuery(id+"F0.imprint","INTERSECT",VERTEX,{"disambiguationData":[OD(0.0)],"derivedFrom":[subQ1,subQ0]});Q15=makeQuery(id+"F0.imprint","IMPRINT",FACE,{"disambiguationData":[TD([[makeQuery(id+"F0.imprint","IMPRINT",EDGE,{"disambiguationData":[TD([[subQ2,1.0]])],"derivedFrom":subQ1}),1.0]])]});}
            var Q16;
            Q16=makeQuery(id+"F0.imprint","IMPRINT",FACE,{"disambiguationData":[TD([[makeQuery(id+"F0.imprint","IMPRINT",EDGE,{"derivedFrom":sQuery(id+"F0.wireOp",EDGE,"E33")}),-1.0]])]});
            var Q17;
            Q17=makeQuery(id+"F0.imprint","IMPRINT",FACE,{"disambiguationData":[TD([[makeQuery(id+"F0.imprint","IMPRINT",EDGE,{"derivedFrom":sQuery(id+"F0.wireOp",EDGE,"E36")}),1.0]])]});
            var Q18;
            {var subQ0=sQuery(id+"F0.wireOp",EDGE,"6d39de08-ad94-4231-b662-17a660603f594.MirrorC");var subQ1=sQuery(id+"F0.wireOp",EDGE,"E44.MirrorC");var subQ2=makeQuery(id+"F0.imprint","INTERSECT",VERTEX,{"disambiguationData":[OD(1.0)],"derivedFrom":[subQ1,subQ0]});Q18=makeQuery(id+"F0.imprint","IMPRINT",FACE,{"disambiguationData":[TD([[makeQuery(id+"F0.imprint","IMPRINT",EDGE,{"disambiguationData":[TD([[subQ2,1.0]])],"derivedFrom":subQ1}),-1.0]])]});}
            var Q19;
            {var subQ0=sQuery(id+"F0.wireOp",EDGE,"6d39de08-ad94-4231-b662-17a660603f594.MirrorC");var subQ1=sQuery(id+"F0.wireOp",EDGE,"E44.MirrorC");var subQ2=makeQuery(id+"F0.imprint","INTERSECT",VERTEX,{"disambiguationData":[OD(0.0)],"derivedFrom":[subQ1,subQ0]});Q19=makeQuery(id+"F0.imprint","IMPRINT",FACE,{"disambiguationData":[TD([[makeQuery(id+"F0.imprint","IMPRINT",EDGE,{"disambiguationData":[TD([[subQ2,-1.0]])],"derivedFrom":subQ1}),1.0]])]});}
            var Q20;
            {var subQ0=sQuery(id+"F0.wireOp",EDGE,"da70cb73-bd24-4d72-8de4-aa27c8984207.MirrorC");var subQ1=sQuery(id+"F0.wireOp",EDGE,"E43");var subQ2=makeQuery(id+"F0.imprint","INTERSECT",VERTEX,{"disambiguationData":[OD(0.0)],"derivedFrom":[subQ1,subQ0]});Q20=makeQuery(id+"F0.imprint","IMPRINT",FACE,{"disambiguationData":[TD([[makeQuery(id+"F0.imprint","IMPRINT",EDGE,{"disambiguationData":[TD([[subQ2,-1.0]])],"derivedFrom":subQ1}),-1.0]])]});}
            var Q21;
            {var subQ0=sQuery(id+"F0.wireOp",EDGE,"E77");var subQ1=sQuery(id+"F0.wireOp",EDGE,"JaYlbfzk-Zl2f-mc1O-yia5-9wafT0kwsFXx");var subQ2=makeQuery(id+"F0.imprint","INTERSECT",VERTEX,{"derivedFrom":[subQ1,subQ0]});Q21=makeQuery(id+"F0.imprint","IMPRINT",FACE,{"disambiguationData":[TD([[makeQuery(id+"F0.imprint","IMPRINT",EDGE,{"disambiguationData":[TD([[subQ2,-1.0]])],"derivedFrom":subQ1}),1.0]])]});}
            var Q22;
            {var subQ0=sQuery(id+"F0.wireOp",EDGE,"E86");var subQ1=sQuery(id+"F0.wireOp",EDGE,"E35");var subQ2=makeQuery(id+"F0.imprint","INTERSECT",VERTEX,{"derivedFrom":[subQ1,subQ0]});Q22=makeQuery(id+"F0.imprint","IMPRINT",FACE,{"disambiguationData":[TD([[makeQuery(id+"F0.imprint","IMPRINT",EDGE,{"disambiguationData":[TD([[subQ2,-1.0]])],"derivedFrom":subQ1}),1.0]])]});}
            var Q23;
            {var subQ3=sQuery(id+"F0.wireOp",EDGE,"E94.filletArc");Q23=makeQuery(id+"F0.imprint","IMPRINT",FACE,{"disambiguationData":[TD([[makeQuery(id+"F0.imprint","IMPRINT",EDGE,{"derivedFrom":subQ3}),-1.0]])]});}
            var Q24;
            {var subQ3=sQuery(id+"F0.wireOp",EDGE,"E93.filletArc");Q24=makeQuery(id+"F0.imprint","IMPRINT",FACE,{"disambiguationData":[TD([[makeQuery(id+"F0.imprint","IMPRINT",EDGE,{"derivedFrom":subQ3}),-1.0]])]});}
            var Q25;
            {var subQ3=sQuery(id+"F0.wireOp",EDGE,"E91.filletArc");Q25=makeQuery(id+"F0.imprint","IMPRINT",FACE,{"disambiguationData":[TD([[makeQuery(id+"F0.imprint","IMPRINT",EDGE,{"derivedFrom":subQ3}),-1.0]])]});}
            var Q26;
            {var subQ3=sQuery(id+"F0.wireOp",EDGE,"E92.filletArc");Q26=makeQuery(id+"F0.imprint","IMPRINT",FACE,{"disambiguationData":[TD([[makeQuery(id+"F0.imprint","IMPRINT",EDGE,{"derivedFrom":subQ3}),-1.0]])]});}
            var Q27;
            {var subQ3=sQuery(id+"F0.wireOp",EDGE,"E90.filletArc");Q27=makeQuery(id+"F0.imprint","IMPRINT",FACE,{"disambiguationData":[TD([[makeQuery(id+"F0.imprint","IMPRINT",EDGE,{"derivedFrom":subQ3}),-1.0]])]});}
            var Q28;
            {var subQ3=sQuery(id+"F0.wireOp",EDGE,"E89.filletArc");Q28=makeQuery(id+"F0.imprint","IMPRINT",FACE,{"disambiguationData":[TD([[makeQuery(id+"F0.imprint","IMPRINT",EDGE,{"derivedFrom":subQ3}),-1.0]])]});}
            var Q29;
            Q29=makeQuery(id+"F0.imprint","IMPRINT",FACE,{"disambiguationData":[TD([[makeQuery(id+"F0.imprint","IMPRINT",EDGE,{"derivedFrom":sQuery(id+"F0.wireOp",EDGE,"E7.MirrorCS")}),1.0]])]});
            var Q30;
            {var subQ0=sQuery(id+"F0.wireOp",EDGE,"PvfX3TML-tEWY-75QP-zgdm-SnZc5ZdSM3lq");Q30=makeQuery(id+"F0.imprint","IMPRINT",FACE,{"disambiguationData":[TD([[makeQuery(id+"F0.imprint","IMPRINT",EDGE,{"derivedFrom":subQ0}),-1.0]])]});}
            var Q31;
            {var subQ0=sQuery(id+"F0.wireOp",EDGE,"VMiJEZT8-RFAT-jsT7-MDdH-zGILJkuwbvlu");Q31=makeQuery(id+"F0.imprint","IMPRINT",FACE,{"disambiguationData":[TD([[makeQuery(id+"F0.imprint","IMPRINT",EDGE,{"derivedFrom":subQ0}),-1.0]])]});}
            var Q32;
            {var subQ0=sQuery(id+"F0.wireOp",EDGE,"E64");Q32=makeQuery(id+"F0.imprint","IMPRINT",FACE,{"disambiguationData":[TD([[makeQuery(id+"F0.imprint","IMPRINT",EDGE,{"derivedFrom":subQ0}),-1.0]])]});}
            var Q33;
            {var subQ5=sQuery(id+"F0.wireOp",EDGE,"VMiJEZT8-RFAT-jsT7-MDdH-zGILJkuwbvlu");Q33=makeQuery(id+"F0.imprint","IMPRINT",FACE,{"disambiguationData":[TD([[makeQuery(id+"F0.imprint","IMPRINT",EDGE,{"derivedFrom":subQ5}),1.0]])]});}
            var Q34;
            Q34=makeQuery(id+"F0.imprint","IMPRINT",FACE,{"disambiguationData":[TD([[makeQuery(id+"F0.imprint","IMPRINT",EDGE,{"derivedFrom":sQuery(id+"F0.wireOp",EDGE,"E43")}),1.0]])]});
            var Q35;
            Q35=makeQuery(id+"F0.imprint","IMPRINT",FACE,{"disambiguationData":[TD([[makeQuery(id+"F0.imprint","IMPRINT",EDGE,{"derivedFrom":sQuery(id+"F0.wireOp",EDGE,"E44.MirrorC")}),-1.0]])]});
            var Q36;
            {var subQ4=sQuery(id+"F0.wireOp",EDGE,"E1.right");Q36=makeQuery(id+"F0.imprint","IMPRINT",FACE,{"disambiguationData":[TD([[makeQuery(id+"F0.imprint","IMPRINT",EDGE,{"derivedFrom":subQ4}),-1.0]])]});}
            var Q37;
            {var subQ1=sQuery(id+"F0.wireOp",EDGE,"VMiJEZT8-RFAT-jsT7-MDdH-zGILJkuwbvlu");var subQ9=sQuery(id+"F0.wireOp",EDGE,"E51.MirrorCS");var subQ10=makeQuery(id+"F0.imprint","INTERSECT",VERTEX,{"derivedFrom":[subQ1,subQ9]});Q37=makeQuery(id+"F0.imprint","IMPRINT",FACE,{"disambiguationData":[TD([[makeQuery(id+"F0.imprint","IMPRINT",EDGE,{"disambiguationData":[TD([[subQ10,1.0]])],"derivedFrom":subQ9}),1.0]])]});}
            var Q38;
            {var subQ0=sQuery(id+"F0.wireOp",EDGE,"E73");var subQ1=sQuery(id+"F0.wireOp",EDGE,"RdLYVHK0-ZMMy-n2T9-vo5N-ViF6aoFnglOa");var subQ2=makeQuery(id+"F0.imprint","INTERSECT",VERTEX,{"derivedFrom":[subQ1,subQ0]});Q38=makeQuery(id+"F0.imprint","IMPRINT",FACE,{"disambiguationData":[TD([[makeQuery(id+"F0.imprint","IMPRINT",EDGE,{"disambiguationData":[TD([[subQ2,-1.0]])],"derivedFrom":subQ1}),1.0]])]});}
            var Q39;
            {var subQ16=sQuery(id+"F0.wireOp",EDGE,"6d39de08-ad94-4231-b662-17a660603f591.MirrorCS");Q39=makeQuery(id+"F0.imprint","IMPRINT",FACE,{"disambiguationData":[TD([[makeQuery(id+"F0.imprint","IMPRINT",EDGE,{"derivedFrom":subQ16}),1.0]])]});}
            var Q40;
            Q40=makeQuery(id+"F0.imprint","IMPRINT",FACE,{"disambiguationData":[TD([[makeQuery(id+"F0.imprint","IMPRINT",EDGE,{"derivedFrom":sQuery(id+"F0.wireOp",EDGE,"E58")}),1.0]])]});
            var Q41;
            {var subQ0=sQuery(id+"F0.wireOp",EDGE,"E9.MirrorCS");Q41=makeQuery(id+"F0.imprint","IMPRINT",FACE,{"disambiguationData":[TD([[makeQuery(id+"F0.imprint","IMPRINT",EDGE,{"derivedFrom":subQ0}),1.0]])]});}
            var Q42;
            Q42=makeQuery(id+"F0.imprint","IMPRINT",FACE,{"disambiguationData":[TD([[makeQuery(id+"F0.imprint","IMPRINT",EDGE,{"derivedFrom":sQuery(id+"F0.wireOp",EDGE,"E37")}),-1.0]])]});
            var Q43;
            Q43=makeQuery(id+"F0.imprint","IMPRINT",FACE,{"disambiguationData":[TD([[makeQuery(id+"F0.imprint","IMPRINT",EDGE,{"derivedFrom":sQuery(id+"F0.wireOp",EDGE,"E0.bottom")}),-1.0]])]});
            var Q44;
            {var subQ6=sQuery(id+"F0.wireOp",EDGE,"E116");Q44=makeQuery(id+"F0.imprint","IMPRINT",FACE,{"disambiguationData":[TD([[makeQuery(id+"F0.imprint","IMPRINT",EDGE,{"derivedFrom":subQ6}),-1.0]])]});}
            var Q45;
            {var subQ0=sQuery(id+"F0.wireOp",EDGE,"E122");Q45=makeQuery(id+"F0.imprint","IMPRINT",FACE,{"disambiguationData":[TD([[makeQuery(id+"F0.imprint","IMPRINT",EDGE,{"derivedFrom":subQ0}),-1.0]])]});}
            var Q46;
            Q46=makeQuery(id+"F0.imprint","IMPRINT",FACE,{"disambiguationData":[TD([[makeQuery(id+"F0.imprint","IMPRINT",EDGE,{"derivedFrom":sQuery(id+"F0.wireOp",EDGE,"E35")}),-1.0]])]});
            var Q47;
            {var subQ0=sQuery(id+"F0.wireOp",EDGE,"E119");Q47=makeQuery(id+"F0.imprint","IMPRINT",FACE,{"disambiguationData":[TD([[makeQuery(id+"F0.imprint","IMPRINT",EDGE,{"derivedFrom":subQ0}),1.0]])]});}
            var Q48;
            {var subQ4=sQuery(id+"F0.wireOp",EDGE,"ruCD1RWU-wJnB-kggX-4DZs-hKizQa8h8jOg");Q48=makeQuery(id+"F0.imprint","IMPRINT",FACE,{"disambiguationData":[TD([[makeQuery(id+"F0.imprint","IMPRINT",EDGE,{"derivedFrom":subQ4}),-1.0]])]});}
            var Q49;
            Q49=makeQuery(id+"F0.imprint","IMPRINT",FACE,{"disambiguationData":[TD([[makeQuery(id+"F0.imprint","IMPRINT",EDGE,{"derivedFrom":sQuery(id+"F0.wireOp",EDGE,"E131")}),-1.0]])]});
            var Q50;
            Q50=makeQuery(id+"F0.imprint","IMPRINT",FACE,{"disambiguationData":[TD([[makeQuery(id+"F0.imprint","IMPRINT",EDGE,{"derivedFrom":sQuery(id+"F0.wireOp",EDGE,"IykK18Gp-FfEv-DaaX-AQvY-SuF3nASqjelH")}),1.0]])]});
            var Q51;
            Q51=makeQuery(id+"F0.imprint","IMPRINT",FACE,{"disambiguationData":[TD([[makeQuery(id+"F0.imprint","IMPRINT",EDGE,{"derivedFrom":sQuery(id+"F0.wireOp",EDGE,"96306cdb-ddaf-400d-b784-63348eaf1cb10.MirrorCS")}),-1.0]])]});
            var Q52;
            Q52=makeQuery(id+"F0.imprint","IMPRINT",FACE,{"disambiguationData":[TD([[makeQuery(id+"F0.imprint","IMPRINT",EDGE,{"derivedFrom":sQuery(id+"F0.wireOp",EDGE,"96306cdb-ddaf-400d-b784-63348eaf1cb12.MirrorC")}),-1.0]])]});
            var Q53;
            {var subQ5=sQuery(id+"F0.wireOp",EDGE,"A3f7MT6z-twOz-Xzec-rXOm-KRLiCk0BcTYY");Q53=makeQuery(id+"F0.imprint","IMPRINT",FACE,{"disambiguationData":[TD([[makeQuery(id+"F0.imprint","IMPRINT",EDGE,{"derivedFrom":subQ5}),-1.0]])]});}
            var Q54;
            Q54=makeQuery(id+"F0.imprint","IMPRINT",FACE,{"disambiguationData":[TD([[makeQuery(id+"F0.imprint","IMPRINT",EDGE,{"derivedFrom":sQuery(id+"F0.wireOp",EDGE,"E157.MirrorCS")}),-1.0]])]});
            var Q55;
            Q55=makeQuery(id+"F0.imprint","IMPRINT",FACE,{"disambiguationData":[TD([[makeQuery(id+"F0.imprint","IMPRINT",EDGE,{"derivedFrom":sQuery(id+"F0.wireOp",EDGE,"4b862817-c2d6-466f-a3c4-4b251d18402a9.MirrorC")}),-1.0]])]});
            var Q56;
            {var subQ9=sQuery(id+"F0.wireOp",EDGE,"E162");Q56=makeQuery(id+"F0.imprint","IMPRINT",FACE,{"disambiguationData":[TD([[makeQuery(id+"F0.imprint","IMPRINT",EDGE,{"derivedFrom":subQ9}),-1.0]])]});}
            var Q57;
            {var subQ0=sQuery(id+"F0.wireOp",EDGE,"E129");Q57=makeQuery(id+"F0.imprint","IMPRINT",FACE,{"disambiguationData":[TD([[makeQuery(id+"F0.imprint","IMPRINT",EDGE,{"derivedFrom":subQ0}),1.0]])]});}
            var Q58;
            {var subQ5=sQuery(id+"F0.wireOp",EDGE,"E162");Q58=makeQuery(id+"F0.imprint","IMPRINT",FACE,{"disambiguationData":[TD([[makeQuery(id+"F0.imprint","IMPRINT",EDGE,{"derivedFrom":subQ5}),1.0]])]});}
            var Q59;
            Q59=makeQuery(id+"F0.imprint","IMPRINT",FACE,{"disambiguationData":[TD([[makeQuery(id+"F0.imprint","IMPRINT",EDGE,{"derivedFrom":sQuery(id+"F0.wireOp",EDGE,"E201.MirrorCS")}),-1.0]])]});
            var Q60;
            Q60=makeQuery(id+"F0.imprint","IMPRINT",FACE,{"disambiguationData":[TD([[makeQuery(id+"F0.imprint","IMPRINT",EDGE,{"derivedFrom":sQuery(id+"F0.wireOp",EDGE,"E189")}),-1.0]])]});
            var Q61;
            Q61=makeQuery(id+"F0.imprint","IMPRINT",FACE,{"disambiguationData":[TD([[makeQuery(id+"F0.imprint","IMPRINT",EDGE,{"derivedFrom":sQuery(id+"F0.wireOp",EDGE,"E8.MirrorCS")}),-1.0]])]});
            var Q62;
            Q62=makeQuery(id+"F0.imprint","IMPRINT",FACE,{"disambiguationData":[TD([[makeQuery(id+"F0.imprint","IMPRINT",EDGE,{"derivedFrom":sQuery(id+"F0.wireOp",EDGE,"E45.MirrorCS")}),1.0]])]});
            var Q63;
            {var subQ0=sQuery(id+"F0.wireOp",EDGE,"E67");var subQ1=sQuery(id+"F0.wireOp",EDGE,"E66");var subQ2=makeQuery(id+"F0.imprint","INTERSECT",VERTEX,{"disambiguationData":[OD(0.0)],"derivedFrom":[subQ1,subQ0]});Q63=makeQuery(id+"F0.imprint","IMPRINT",FACE,{"disambiguationData":[TD([[makeQuery(id+"F0.imprint","IMPRINT",EDGE,{"disambiguationData":[TD([[subQ2,-1.0]])],"derivedFrom":subQ1}),1.0]])]});}
            var Q64;
            {var subQ0=sQuery(id+"F0.wireOp",EDGE,"E67");var subQ1=sQuery(id+"F0.wireOp",EDGE,"E66");var subQ2=makeQuery(id+"F0.imprint","INTERSECT",VERTEX,{"disambiguationData":[OD(0.0)],"derivedFrom":[subQ1,subQ0]});Q64=makeQuery(id+"F0.imprint","IMPRINT",FACE,{"disambiguationData":[TD([[makeQuery(id+"F0.imprint","IMPRINT",EDGE,{"disambiguationData":[TD([[subQ2,-1.0]])],"derivedFrom":subQ1}),-1.0]])]});}
            var Q65;
            {var subQ4=sQuery(id+"F0.wireOp",EDGE,"E32");var subQ5=sQuery(id+"F0.wireOp",EDGE,"E1.bottom");var subQ6=makeQuery(id+"F0.imprint","INTERSECT",VERTEX,{"derivedFrom":[subQ5,subQ4]});Q65=makeQuery(id+"F0.imprint","IMPRINT",FACE,{"disambiguationData":[TD([[makeQuery(id+"F0.imprint","IMPRINT",EDGE,{"disambiguationData":[TD([[subQ6,-1.0]])],"derivedFrom":subQ5}),-1.0]])]});}
            extrude(context, id + "F1", {"entities" : qUnion([Q0, Q1, Q2, Q3, Q4, Q5, Q6, Q7, Q8, Q9, Q10, Q11, Q12, Q13, Q14, Q15, Q16, Q17, Q18, Q19, Q20, Q21, Q22, Q23, Q24, Q25, Q26, Q27, Q28, Q29, Q30, Q31, Q32, Q33, Q34, Q35, Q36, Q37, Q38, Q39, Q40, Q41, Q42, Q43, Q44, Q45, Q46, Q47, Q48, Q49, Q50, Q51, Q52, Q53, Q54, Q55, Q56, Q57, Q58, Q59, Q60, Q61, Q62, Q63, Q64, Q65]), "oppositeDirection" : true, "depth" : 30 * mm, "offsetDistance" : 25 * mm});
        }
        {
            var Q0;
            {var subQ0=sQuery(id+"F0.wireOp",EDGE,"E32");var subQ1=sQuery(id+"F0.wireOp",EDGE,"E1.bottom");var subQ2=makeQuery(id+"F0.imprint","INTERSECT",VERTEX,{"derivedFrom":[subQ1,subQ0]});Q0=makeQuery(id+"F0.imprint","IMPRINT",FACE,{"disambiguationData":[TD([[makeQuery(id+"F0.imprint","IMPRINT",EDGE,{"disambiguationData":[TD([[subQ2,-1.0]])],"derivedFrom":subQ1}),-1.0]])]});}
            extrude(context, id + "F2", {"entities" : qUnion([Q0]), "operationType" : NewBodyOperationType.ADD, "oppositeDirection" : true, "depth" : 3 * mm, "offsetDistance" : 25 * mm});
        }
        {
            var Q0;
            Q0=makeQuery(id+"F0.imprint","IMPRINT",FACE,{"disambiguationData":[TD([[makeQuery(id+"F0.imprint","IMPRINT",EDGE,{"derivedFrom":sQuery(id+"F0.wireOp",EDGE,"E26")}),-1.0]])]});
            extrude(context, id + "F3", {"entities" : qUnion([Q0]), "operationType" : NewBodyOperationType.ADD, "oppositeDirection" : true, "depth" : 10 * mm, "offsetDistance" : 25 * mm});
        }
        {
            var Q0;
            Q0=makeQuery(id+"F0.imprint","IMPRINT",FACE,{"disambiguationData":[TD([[makeQuery(id+"F0.imprint","IMPRINT",EDGE,{"derivedFrom":sQuery(id+"F0.wireOp",EDGE,"E14.left")}),1.0]])]});
            var Q1;
            {var subQ2=sQuery(id+"F0.wireOp",EDGE,"E23");Q1=makeQuery(id+"F0.imprint","IMPRINT",FACE,{"disambiguationData":[TD([[makeQuery(id+"F0.imprint","IMPRINT",EDGE,{"derivedFrom":subQ2}),-1.0]])]});}
            var Q2;
            {var subQ0=sQuery(id+"F0.wireOp",EDGE,"E23");Q2=makeQuery(id+"F0.imprint","IMPRINT",FACE,{"disambiguationData":[TD([[makeQuery(id+"F0.imprint","IMPRINT",EDGE,{"derivedFrom":subQ0}),1.0]])]});}
            var Q3;
            {var subQ3=sQuery(id+"F0.wireOp",EDGE,"E25");Q3=makeQuery(id+"F0.imprint","IMPRINT",FACE,{"disambiguationData":[TD([[makeQuery(id+"F0.imprint","IMPRINT",EDGE,{"derivedFrom":subQ3}),1.0]])]});}
            var Q4;
            Q4=makeQuery(id+"F0.imprint","IMPRINT",FACE,{"disambiguationData":[TD([[makeQuery(id+"F0.imprint","IMPRINT",EDGE,{"derivedFrom":sQuery(id+"F0.wireOp",EDGE,"E20")}),-1.0]])]});
            var Q5;
            {var subQ0=sQuery(id+"F0.wireOp",EDGE,"E63");Q5=makeQuery(id+"F0.imprint","IMPRINT",FACE,{"disambiguationData":[TD([[makeQuery(id+"F0.imprint","IMPRINT",EDGE,{"derivedFrom":subQ0}),-1.0]])]});}
            extrude(context, id + "F4", {"entities" : qUnion([Q0, Q1, Q2, Q3, Q4, Q5]), "oppositeDirection" : true, "depth" : 30 * mm, "offsetDistance" : 25 * mm});
        }
        {
            var Q0;
            {var subQ1=sQuery(id+"F0.wireOp",EDGE,"E23");Q0=makeQuery(id+"F0.imprint","IMPRINT",FACE,{"disambiguationData":[TD([[makeQuery(id+"F0.imprint","IMPRINT",EDGE,{"derivedFrom":subQ1}),1.0]])]});}
            extrude(context, id + "F5", {"entities" : qUnion([Q0]), "operationType" : NewBodyOperationType.REMOVE, "oppositeDirection" : true, "depth" : 10 * mm, "offsetDistance" : 25 * mm});
        }
        {
            var Q0;
            Q0=makeQuery(id+"F0.imprint","IMPRINT",FACE,{"disambiguationData":[TD([[makeQuery(id+"F0.imprint","IMPRINT",EDGE,{"derivedFrom":sQuery(id+"F0.wireOp",EDGE,"E17.MirrorC")}),1.0]])]});
            var Q1;
            Q1=makeQuery(id+"F0.imprint","IMPRINT",FACE,{"disambiguationData":[TD([[makeQuery(id+"F0.imprint","IMPRINT",EDGE,{"derivedFrom":sQuery(id+"F0.wireOp",EDGE,"E15")}),-1.0]])]});
            extrude(context, id + "F6", {"entities" : qUnion([Q0, Q1]), "operationType" : NewBodyOperationType.ADD, "oppositeDirection" : true, "depth" : 5 * mm, "offsetDistance" : 25 * mm});
        }
        {
            var Q0;
            Q0=makeQuery(id+"F1.opExtrude","SWEPT_FACE",FACE,{"disambiguationData":[OSD([sQuery(id+"F0.wireOp",EDGE,"E1.left"),sQuery(id+"F0.wireOp",EDGE,"E4.MirrorCS"),sQuery(id+"F0.wireOp",EDGE,"E12"),sQuery(id+"F0.wireOp",EDGE,"E13")])]});
            var sketch = newSketch(context, id + "F7", { "sketchPlane" : qUnion([Q0])});
            skLineSegment(sketch, "E214", {"start": v(-67, -30) * mm, "end": v(-67, 0) * mm});
            skFitSpline(sketch, "E215", {"points": [v(-67, -30) * mm, v(-71.65, -23.82) * mm, v(-73.03, -16.23) * mm, v(-74.55, -9.18) * mm, v(-80, -1.17) * mm], "startDerivative": vector(-22.4, 23.58) * mm, "endDerivative": vector(-23.42, 29.28) * mm});
            skLineSegment(sketch, "E216", {"start": v(-67, -30) * mm, "end": v(-80, -30) * mm});
            skLineSegment(sketch, "E217", {"start": v(-80, -30) * mm, "end": v(-80, -1.17) * mm});
            skLineSegment(sketch, "E218.MirrorCS", {"start": v(67, -30) * mm, "end": v(80, -30) * mm});
            skFitSpline(sketch, "E219.MirrorCS", {"points": [v(67, -30) * mm, v(71.65, -23.82) * mm, v(73.03, -16.23) * mm, v(74.55, -9.18) * mm, v(80, -1.17) * mm], "startDerivative": vector(22.4, 23.58) * mm, "endDerivative": vector(23.42, 29.28) * mm});
            skLineSegment(sketch, "E220.MirrorCS", {"start": v(80, -30) * mm, "end": v(80, -1.17) * mm});
            skLineSegment(sketch, "E221.MirrorCS", {"start": v(67, -30) * mm, "end": v(67, 0) * mm});
            skSolve(sketch);
        }
        {
            var Q0;
            Q0=makeQuery(id+"F7.imprint","IMPRINT",FACE,{"disambiguationData":[TD([[makeQuery(id+"F7.imprint","IMPRINT",EDGE,{"derivedFrom":sQuery(id+"F7.wireOp",EDGE,"E220.MirrorCS")}),1.0]])]});
            var Q1;
            Q1=makeQuery(id+"F7.imprint","IMPRINT",FACE,{"disambiguationData":[TD([[makeQuery(id+"F7.imprint","IMPRINT",EDGE,{"derivedFrom":sQuery(id+"F7.wireOp",EDGE,"E215")}),1.0]])]});
            extrude(context, id + "F8", {"entities" : qUnion([Q0, Q1]), "operationType" : NewBodyOperationType.REMOVE, "oppositeDirection" : true, "depth" : 200 * mm, "offsetDistance" : 25 * mm});
        }
        {
            var Q0;
            Q0=qCreatedBy(makeId("Front.planeOp"),FACE);
            var sketch = newSketch(context, id + "F9", { "sketchPlane" : qUnion([Q0])});
            skLineSegment(sketch, "E222", {"start": v(79.29, -30) * mm, "end": v(79.29, 0) * mm});
            skFitSpline(sketch, "E223.MirrorCS", {"points": [v(79.59, -30) * mm, v(84.24, -23.83) * mm, v(85.62, -16.23) * mm, v(87.14, -9.18) * mm, v(92.59, -1.17) * mm], "startDerivative": vector(22.4, 23.58) * mm, "endDerivative": vector(23.42, 29.28) * mm});
            skLineSegment(sketch, "E224.MirrorCS", {"start": v(79.59, -30) * mm, "end": v(92.59, -30) * mm});
            skLineSegment(sketch, "E225.MirrorCS", {"start": v(92.59, -30) * mm, "end": v(92.59, -1.17) * mm});
            skSolve(sketch);
        }
        {
            var Q0;
            Q0=qSketchRegion(id+"F9",true);
            extrude(context, id + "F10", {"entities" : qUnion([Q0]), "operationType" : NewBodyOperationType.REMOVE, "oppositeDirection" : true, "depth" : 90 * mm, "offsetDistance" : 25 * mm, "hasSecondDirection" : true, "secondDirectionOppositeDirection" : false, "secondDirectionDepth" : 90 * mm});
        }
        {
            var Q0;
            Q0=makeQuery(id+"F4.opExtrude","SWEPT_FACE",FACE,{"disambiguationData":[OSD([sQuery(id+"F0.wireOp",EDGE,"E28"),sQuery(id+"F0.wireOp",EDGE,"E29")])]});
            var sketch = newSketch(context, id + "F11", { "sketchPlane" : qUnion([Q0])});
            skLineSegment(sketch, "E226", {"start": v(-67.14, -30) * mm, "end": v(-67.14, 0) * mm});
            skFitSpline(sketch, "E227", {"points": [v(-67.14, -30) * mm, v(-71.8, -23.82) * mm, v(-73.17, -16.23) * mm, v(-74.7, -9.18) * mm, v(-80.14, -1.17) * mm], "startDerivative": vector(-22.4, 23.58) * mm, "endDerivative": vector(-23.42, 29.28) * mm});
            skLineSegment(sketch, "E228", {"start": v(-67.14, -30) * mm, "end": v(-80.14, -30) * mm});
            skLineSegment(sketch, "E229", {"start": v(-80.14, -30) * mm, "end": v(-80.14, -1.17) * mm});
            skLineSegment(sketch, "E230.MirrorCS", {"start": v(67.06, -30) * mm, "end": v(67.06, 0) * mm});
            skLineSegment(sketch, "E231.MirrorCS", {"start": v(67.06, -30) * mm, "end": v(80.06, -30) * mm});
            skFitSpline(sketch, "E232.MirrorCS", {"points": [v(67.06, -30) * mm, v(71.7, -23.82) * mm, v(73.09, -16.23) * mm, v(74.6, -9.18) * mm, v(80.06, -1.17) * mm], "startDerivative": vector(22.4, 23.58) * mm, "endDerivative": vector(23.42, 29.28) * mm});
            skLineSegment(sketch, "E233", {"start": v(80.06, -30) * mm, "end": v(80.06, -1.17) * mm});
            skSolve(sketch);
        }
        {
            var Q0;
            {var subQ3=sQuery(id+"F11.wireOp",EDGE,"E233");Q0=makeQuery(id+"F11.imprint","IMPRINT",FACE,{"disambiguationData":[TD([[makeQuery(id+"F11.imprint","IMPRINT",EDGE,{"derivedFrom":subQ3}),1.0]])]});}
            var Q1;
            {var subQ0=sQuery(id+"F11.wireOp",EDGE,"E231.MirrorCS");var subQ1=sQuery(id+"F0.wireOp",EDGE,"E29");var subQ2=makeQuery(id+"F4.opExtrude","SWEPT_EDGE",EDGE,{"disambiguationData":[OSD([subQ1,sQuery(id+"F0.wireOp",EDGE,"E60")])]});var subQ3=makeQuery(id+"F11.imprint","INTERSECT",VERTEX,{"derivedFrom":[subQ2,subQ0]});Q1=makeQuery(id+"F11.imprint","IMPRINT",FACE,{"disambiguationData":[TD([[makeQuery(id+"F11.imprint","IMPRINT",EDGE,{"disambiguationData":[TD([[subQ3,-1.0]])],"derivedFrom":subQ2}),1.0]])]});}
            var Q2;
            Q2=makeQuery(id+"F11.imprint","IMPRINT",FACE,{"disambiguationData":[TD([[makeQuery(id+"F11.imprint","IMPRINT",EDGE,{"derivedFrom":sQuery(id+"F11.wireOp",EDGE,"E227")}),1.0]])]});
            extrude(context, id + "F12", {"entities" : qUnion([Q0, Q1, Q2]), "operationType" : NewBodyOperationType.REMOVE, "oppositeDirection" : true, "depth" : 50 * mm, "offsetDistance" : 25 * mm});
        }
        {
            var Q0;
            Q0=makeQuery(id+"F4.opExtrude","CAP_EDGE",EDGE,{"disambiguationData":[OSD([sQuery(id+"F0.wireOp",EDGE,"E62")])],"isStart":false});
            var Q1;
            Q1=makeQuery(id+"F4.opExtrude","CAP_EDGE",EDGE,{"disambiguationData":[OSD([sQuery(id+"F0.wireOp",EDGE,"E14.left"),sQuery(id+"F0.wireOp",EDGE,"E19.MirrorCS"),sQuery(id+"F0.wireOp",EDGE,"E113")])],"isStart":false});
            var Q2;
            Q2=makeQuery(id+"F4.opExtrude","CAP_EDGE",EDGE,{"disambiguationData":[OSD([sQuery(id+"F0.wireOp",EDGE,"E63")])],"isStart":false});
            fillet(context, id + "F13", {"entities" : qUnion([Q0, Q1, Q2]), "radius" : 20 * mm, "tangentPropagation" : true, "allowEdgeOverflow" : false});
        }
    });
